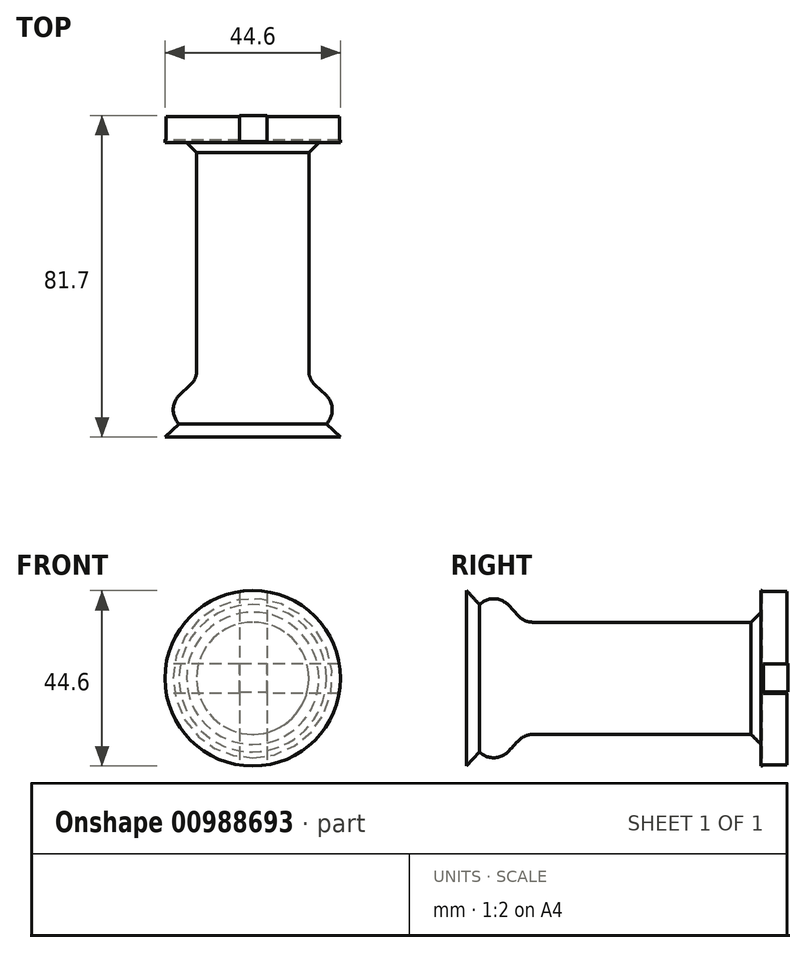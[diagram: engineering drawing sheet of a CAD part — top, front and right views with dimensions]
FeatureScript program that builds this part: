
annotation { "Feature Type Name" : "Feature", "Feature Type Description" : "" }
export const myFeature = defineFeature(function(context is Context, id is Id, definition is map)
    precondition{}
    {
        {
            var Q0;
            Q0=qCreatedBy(makeId("Top.planeOp"),FACE);
            var sketch = newSketch(context, id + "F0", { "sketchPlane" : qUnion([Q0])});
            skLineSegment(sketch, "E0", {"start": v(0, 47.92) * mm, "end": v(22.3, 47.92) * mm});
            skLineSegment(sketch, "E1", {"start": v(22.3, 47.92) * mm, "end": v(22.3, 41.3) * mm});
            skLineSegment(sketch, "E2", {"start": v(22.3, 41.3) * mm, "end": v(14.25, 41.3) * mm});
            skLineSegment(sketch, "E3", {"start": v(14.25, 41.3) * mm, "end": v(14.25, -18.85) * mm});
            skLineSegment(sketch, "E4", {"start": v(14.25, -18.85) * mm, "end": v(22.3, -26.33) * mm});
            skLineSegment(sketch, "E5", {"start": v(22.3, -26.33) * mm, "end": v(18.72, -30.2) * mm});
            skLineSegment(sketch, "E6", {"start": v(18.72, -30.2) * mm, "end": v(22.3, -33.53) * mm});
            skLineSegment(sketch, "E7", {"start": v(22.3, -33.53) * mm, "end": v(0, -33.53) * mm});
            skLineSegment(sketch, "E8", {"start": v(0, 47.92) * mm, "end": v(0, -33.53) * mm});
            skSolve(sketch);
        }
        {
            var Q0;
            Q0 = qSketchRegion(id + "F0", true);
            var Q1;
            Q1=sQuery(id+"F0.wireOp",EDGE,"E8");
            revolve(context, id + "F1", {"surfaceOperationType" : NewSurfaceOperationType.NEW, "entities" : qUnion([Q0]), "axis" : qUnion([Q1]), "revolveType" : RevolveType.FULL});
        }
        {
            var Q0;
            Q0=makeQuery(id+"F1.opRevolve","SWEPT_EDGE",EDGE,{"disambiguationData":[OSD([sQuery(id+"F0.wireOp",EDGE,"E4"),sQuery(id+"F0.wireOp",EDGE,"E5")])]});
            var Q1;
            Q1=makeQuery(id+"F1.opRevolve","SWEPT_EDGE",EDGE,{"disambiguationData":[OSD([sQuery(id+"F0.wireOp",EDGE,"E3"),sQuery(id+"F0.wireOp",EDGE,"E4")])]});
            fillet(context, id + "F2", {"entities" : qUnion([Q0, Q1]), "radius" : 5.08 * mm, "tangentPropagation" : true, "allowEdgeOverflow" : false});
        }
        {
            var Q0;
            Q0=makeQuery(id+"F1.opRevolve","SWEPT_FACE",FACE,{"disambiguationData":[OSD([sQuery(id+"F0.wireOp",EDGE,"E3")])]});
            chamfer(context, id + "F3", {"entities" : qUnion([Q0]), "width" : 2.54 * mm, "tangentPropagation" : true});
        }
        {
            var Q0;
            Q0=makeQuery(id+"F1.opRevolve","SWEPT_FACE",FACE,{"disambiguationData":[OSD([sQuery(id+"F0.wireOp",EDGE,"E0")])]});
            var sketch = newSketch(context, id + "F4", { "sketchPlane" : qUnion([Q0])});
            skLineSegment(sketch, "E9.bottom", {"start": v(-3.6, 26.33) * mm, "end": v(3.3, 26.33) * mm});
            skLineSegment(sketch, "E9.top", {"start": v(-3.6, -25.18) * mm, "end": v(3.3, -25.18) * mm});
            skLineSegment(sketch, "E9.left", {"start": v(-3.6, 26.33) * mm, "end": v(-3.6, -25.18) * mm});
            skLineSegment(sketch, "E9.right", {"start": v(3.3, 26.33) * mm, "end": v(3.3, -25.18) * mm});
            skSolve(sketch);
        }
        {
            var Q0;
            Q0 = qSketchRegion(id + "F4", true);
            extrude(context, id + "F5", {"entities" : qUnion([Q0]), "operationType" : NewBodyOperationType.REMOVE, "oppositeDirection" : true, "depth" : 6.35 * mm, "offsetDistance" : 25.4 * mm});
        }
        {
            var Q0;
            Q0=makeQuery(id+"F5.boolean.opBoolean","SPLIT",FACE,{"disambiguationData":[TD([makeQuery(id+"F5.opExtrude","SWEPT_FACE",FACE,{"disambiguationData":[OSD([sQuery(id+"F4.wireOp",EDGE,"E9.left")])]})])],"derivedFrom":makeQuery(id+"F1.opRevolve","SWEPT_FACE",FACE,{"disambiguationData":[OSD([sQuery(id+"F0.wireOp",EDGE,"E0")])]})});
            var sketch = newSketch(context, id + "F6", { "sketchPlane" : qUnion([Q0])});
            skLineSegment(sketch, "E10.bottom", {"start": v(-25.76, 3.6) * mm, "end": v(26.33, 3.6) * mm});
            skLineSegment(sketch, "E10.top", {"start": v(-25.76, -3.89) * mm, "end": v(26.33, -3.89) * mm});
            skLineSegment(sketch, "E10.left", {"start": v(-25.76, 3.6) * mm, "end": v(-25.76, -3.89) * mm});
            skLineSegment(sketch, "E10.right", {"start": v(26.33, 3.6) * mm, "end": v(26.33, -3.89) * mm});
            skSolve(sketch);
        }
        {
            var Q0;
            Q0 = qSketchRegion(id + "F6", true);
            extrude(context, id + "F7", {"entities" : qUnion([Q0]), "operationType" : NewBodyOperationType.REMOVE, "oppositeDirection" : true, "depth" : 5.94 * mm, "offsetDistance" : 25.4 * mm});
        }
        {
            var Q0;
            Q0=makeQuery(id+"F5.boolean.opBoolean","COPY",FACE,{"derivedFrom":makeQuery(id+"F5.opExtrude","CAP_FACE",FACE,{"disambiguationData":[OSD([sQuery(id+"F4.wireOp",EDGE,"E9.bottom"),sQuery(id+"F4.wireOp",EDGE,"E9.top"),sQuery(id+"F4.wireOp",EDGE,"E9.left"),sQuery(id+"F4.wireOp",EDGE,"E9.right")])],"isStart":false})});
            var sketch = newSketch(context, id + "F8", { "sketchPlane" : qUnion([Q0])});
            skLineSegment(sketch, "E11", {"start": v(3.3, -3.52) * mm, "end": v(-3.6, -3.52) * mm});
            skLineSegment(sketch, "E12", {"start": v(3.3, -3.52) * mm, "end": v(3.3, 3.76) * mm});
            skLineSegment(sketch, "E13", {"start": v(3.3, 3.76) * mm, "end": v(-3.6, 3.76) * mm});
            skLineSegment(sketch, "E14", {"start": v(-3.6, 3.76) * mm, "end": v(-3.6, -3.52) * mm});
            skSolve(sketch);
        }
        {
            var Q0;
            Q0 = qSketchRegion(id + "F8", true);
            extrude(context, id + "F9", {"entities" : qUnion([Q0]), "operationType" : NewBodyOperationType.ADD, "depth" : 6.6 * mm, "offsetDistance" : 25.4 * mm});
        }
    });
